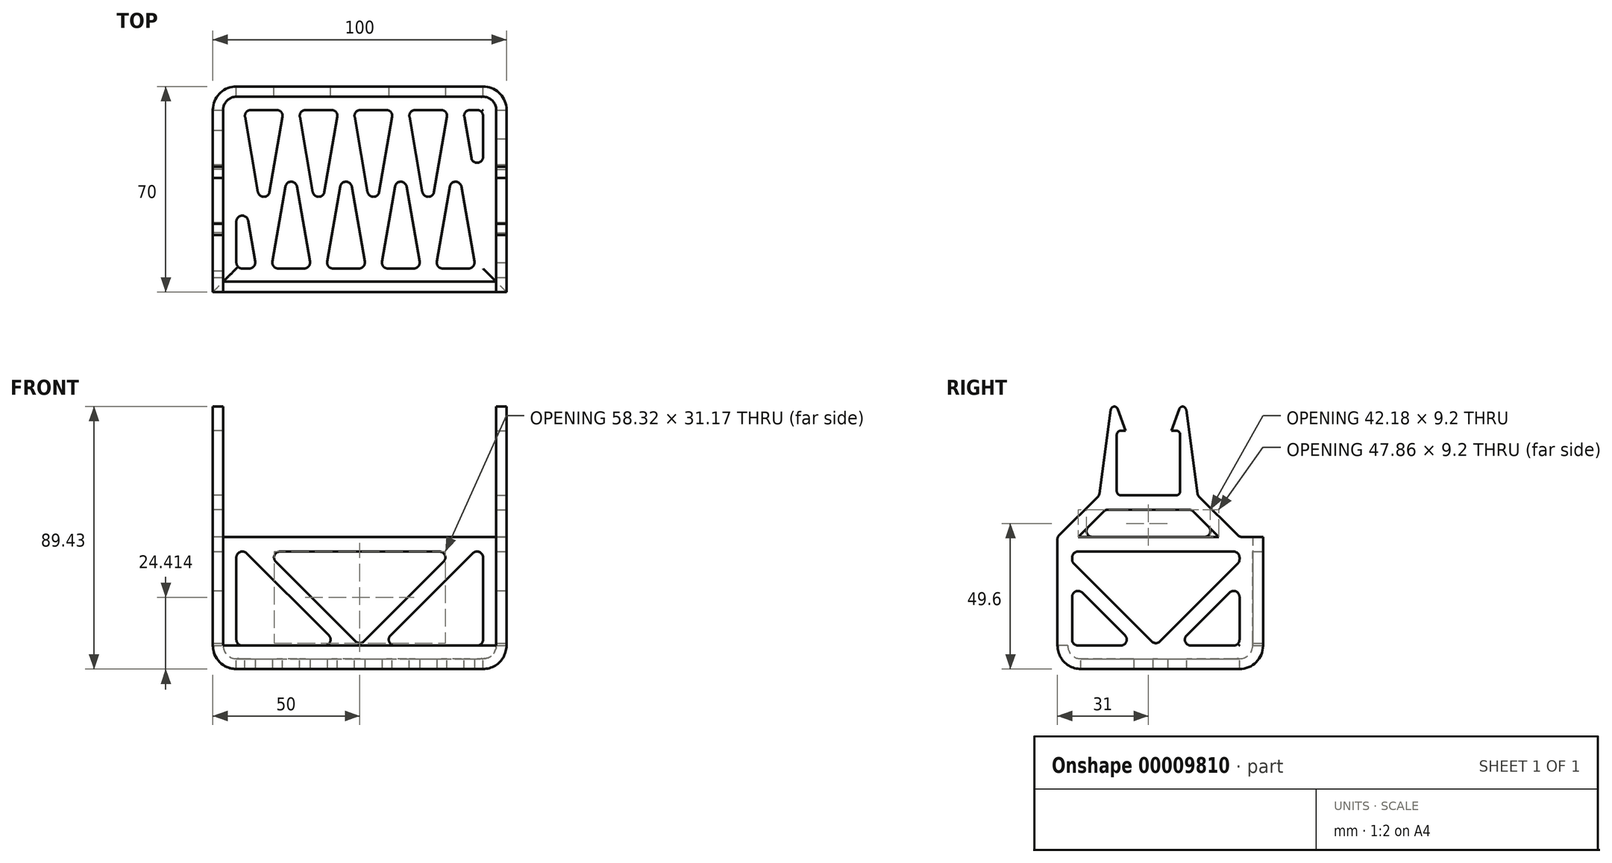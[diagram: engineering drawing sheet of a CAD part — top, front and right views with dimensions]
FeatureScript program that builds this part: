
annotation { "Feature Type Name" : "Feature", "Feature Type Description" : "" }
export const myFeature = defineFeature(function(context is Context, id is Id, definition is map)
    precondition{}
    {
        {
            var Q0;
            Q0=qCreatedBy(makeId("Top.planeOp"),FACE);
            var sketch = newSketch(context, id + "F0", { "sketchPlane" : qUnion([Q0])});
            skLineSegment(sketch, "E0.rect.bottom", {"start": v(50, 35) * mm, "end": v(-50, 35) * mm});
            skLineSegment(sketch, "E0.rect.top", {"start": v(50, -35) * mm, "end": v(-50, -35) * mm});
            skLineSegment(sketch, "E0.rect.left", {"start": v(50, 35) * mm, "end": v(50, -35) * mm});
            skLineSegment(sketch, "E0.rect.right", {"start": v(-50, 35) * mm, "end": v(-50, -35) * mm});
            skPoint(sketch, "E0.rect.middle", {"position": v(0, 0) * mm});
            skSolve(sketch);
        }
        {
            var Q0;
            Q0 = qSketchRegion(id + "F0", true);
            extrude(context, id + "F1", {"entities" : qUnion([Q0]), "depth" : 45 * mm});
        }
        {
            var Q0;
            Q0=makeQuery(id+"F1.opExtrude","CAP_FACE",FACE,{"disambiguationData":[OSD([sQuery(id+"F0.wireOp",EDGE,"E0.rect.bottom"),sQuery(id+"F0.wireOp",EDGE,"E0.rect.top"),sQuery(id+"F0.wireOp",EDGE,"E0.rect.left"),sQuery(id+"F0.wireOp",EDGE,"E0.rect.right")])],"isStart":true});
            var Q1;
            Q1=makeQuery(id+"F1.opExtrude","SWEPT_EDGE",EDGE,{"disambiguationData":[OSD([sQuery(id+"F0.wireOp",EDGE,"E0.rect.bottom"),sQuery(id+"F0.wireOp",EDGE,"E0.rect.left")])]});
            var Q2;
            Q2=makeQuery(id+"F1.opExtrude","SWEPT_EDGE",EDGE,{"disambiguationData":[OSD([sQuery(id+"F0.wireOp",EDGE,"E0.rect.bottom"),sQuery(id+"F0.wireOp",EDGE,"E0.rect.right")])]});
            fillet(context, id + "F2", {"entities" : qUnion([Q0, Q1, Q2]), "radius" : 8 * mm, "tangentPropagation" : true, "allowEdgeOverflow" : false});
        }
        {
            var Q0;
            Q0=makeQuery(id+"F1.opExtrude","CAP_FACE",FACE,{"disambiguationData":[OSD([sQuery(id+"F0.wireOp",EDGE,"E0.rect.bottom"),sQuery(id+"F0.wireOp",EDGE,"E0.rect.top"),sQuery(id+"F0.wireOp",EDGE,"E0.rect.left"),sQuery(id+"F0.wireOp",EDGE,"E0.rect.right")])],"isStart":false});
            shell(context, id + "F3", {"entities" : qUnion([Q0]), "thickness" : 3.5 * mm});
        }
        {
            var Q0;
            Q0=makeQuery(id+"F1.opExtrude","SWEPT_FACE",FACE,{"disambiguationData":[OSD([sQuery(id+"F0.wireOp",EDGE,"E0.rect.top")])]});
            var sketch = newSketch(context, id + "F4", { "sketchPlane" : qUnion([Q0])});
            skLineSegment(sketch, "E1.0", {"start": v(-46.5, 45) * mm, "end": v(-46.5, 8) * mm});
            skLineSegment(sketch, "E2.0", {"start": v(46.5, 8) * mm, "end": v(46.5, 45) * mm});
            skLineSegment(sketch, "E3", {"start": v(-46.5, 45) * mm, "end": v(46.5, 45) * mm});
            skLineSegment(sketch, "E4", {"start": v(46.5, 8) * mm, "end": v(-46.5, 8) * mm});
            skSolve(sketch);
        }
        {
            var Q0;
            {var subQ3=sQuery(id+"F4.wireOp",EDGE,"E1.0");Q0=makeQuery(id+"F4.imprint","IMPRINT",FACE,{"disambiguationData":[TD([[makeQuery(id+"F4.imprint","IMPRINT",EDGE,{"derivedFrom":subQ3}),1.0]])]});}
            var Q1;
            {var subQ0=sQuery(id+"F0.wireOp",EDGE,"E0.rect.top");var subQ1=makeQuery(id+"F1.opExtrude","SWEPT_FACE",FACE,{"disambiguationData":[OSD([subQ0])]});var subQ2=makeQuery(id+"F2.opFillet","BLEND_EDGE",EDGE,{"blendedFrom":[makeQuery(id+"F1.opExtrude","SWEPT_EDGE",EDGE,{"disambiguationData":[OSD([subQ0,sQuery(id+"F0.wireOp",EDGE,"E0.rect.left")])]}),subQ1],"blendedInto":[subQ1]});Q1=makeQuery(id+"F4.imprint","IMPRINT",FACE,{"disambiguationData":[TD([[makeQuery(id+"F4.imprint","IMPRINT",EDGE,{"derivedFrom":subQ2}),1.0]])]});}
            var Q2;
            {var subQ3=sQuery(id+"F4.wireOp",EDGE,"E2.0");Q2=makeQuery(id+"F4.imprint","IMPRINT",FACE,{"disambiguationData":[TD([[makeQuery(id+"F4.imprint","IMPRINT",EDGE,{"derivedFrom":subQ3}),1.0]])]});}
            extrude(context, id + "F5", {"entities" : qUnion([Q0, Q1, Q2]), "operationType" : NewBodyOperationType.REMOVE, "oppositeDirection" : true, "depth" : 25.4 * mm});
        }
        {
            var Q0;
            Q0=makeQuery(id+"F1.opExtrude","SWEPT_FACE",FACE,{"disambiguationData":[OSD([sQuery(id+"F0.wireOp",EDGE,"E0.rect.left")])]});
            var sketch = newSketch(context, id + "F6", { "sketchPlane" : qUnion([Q0])});
            skLineSegment(sketch, "E5", {"start": v(-30, 45) * mm, "end": v(-30, 8) * mm});
            skLineSegment(sketch, "E6", {"start": v(27, 45) * mm, "end": v(27, 8) * mm});
            skLineSegment(sketch, "E7", {"start": v(27, 8) * mm, "end": v(32, 8) * mm});
            skLineSegment(sketch, "E8", {"start": v(32, 8) * mm, "end": v(32, 45) * mm});
            skLineSegment(sketch, "E9", {"start": v(-35, 45) * mm, "end": v(-35, 8) * mm});
            skLineSegment(sketch, "E10", {"start": v(-35, 8) * mm, "end": v(-30, 8) * mm});
            skLineSegment(sketch, "E11", {"start": v(-30, 40) * mm, "end": v(27, 40) * mm});
            skLineSegment(sketch, "E12", {"start": v(27, 40) * mm, "end": v(27, 45) * mm});
            skLineSegment(sketch, "E13", {"start": v(-30, 8) * mm, "end": v(27, 8) * mm});
            skLineSegment(sketch, "E14", {"start": v(-1.5, 40) * mm, "end": v(-1.5, 8) * mm, "construction": true});
            skLineSegment(sketch, "E15", {"start": v(-1.5, 40) * mm, "end": v(-1.5, 45) * mm, "construction": true});
            skLineSegment(sketch, "E16", {"start": v(-1.5, 8) * mm, "end": v(-30, 36.5) * mm});
            skLineSegment(sketch, "E17", {"start": v(-8.57, 8) * mm, "end": v(-30, 29.43) * mm});
            skLineSegment(sketch, "E18", {"start": v(-15.75, 22.25) * mm, "end": v(-19.29, 18.71) * mm, "construction": true});
            skLineSegment(sketch, "E19", {"start": v(-1.5, 8) * mm, "end": v(27, 36.5) * mm});
            skLineSegment(sketch, "E20", {"start": v(5.57, 8) * mm, "end": v(27, 29.43) * mm});
            skLineSegment(sketch, "E21", {"start": v(12.75, 22.25) * mm, "end": v(16.29, 18.71) * mm, "construction": true});
            skSolve(sketch);
        }
        {
            var Q0;
            {var subQ0=sQuery(id+"F6.wireOp",EDGE,"E17");Q0=makeQuery(id+"F6.imprint","IMPRINT",FACE,{"disambiguationData":[TD([[makeQuery(id+"F6.imprint","IMPRINT",EDGE,{"derivedFrom":subQ0}),1.0]])]});}
            var Q1;
            {var subQ2=sQuery(id+"F6.wireOp",EDGE,"E11");Q1=makeQuery(id+"F6.imprint","IMPRINT",FACE,{"disambiguationData":[TD([[makeQuery(id+"F6.imprint","IMPRINT",EDGE,{"derivedFrom":subQ2}),-1.0]])]});}
            var Q2;
            {var subQ0=sQuery(id+"F6.wireOp",EDGE,"E20");Q2=makeQuery(id+"F6.imprint","IMPRINT",FACE,{"disambiguationData":[TD([[makeQuery(id+"F6.imprint","IMPRINT",EDGE,{"derivedFrom":subQ0}),-1.0]])]});}
            extrude(context, id + "F7", {"entities" : qUnion([Q0, Q1, Q2]), "operationType" : NewBodyOperationType.REMOVE, "endBound" : BoundingType.THROUGH_ALL, "oppositeDirection" : true, "depth" : 25.4 * mm});
        }
        {
            var Q0;
            Q0=makeQuery(id+"F1.opExtrude","SWEPT_FACE",FACE,{"disambiguationData":[OSD([sQuery(id+"F0.wireOp",EDGE,"E0.rect.bottom")])]});
            var sketch = newSketch(context, id + "F8", { "sketchPlane" : qUnion([Q0])});
            skLineSegment(sketch, "E22", {"start": v(-42, 45) * mm, "end": v(-42, 8) * mm});
            skLineSegment(sketch, "E23", {"start": v(-42, 8) * mm, "end": v(-47, 8) * mm});
            skLineSegment(sketch, "E24", {"start": v(-47, 8) * mm, "end": v(-47, 45) * mm});
            skLineSegment(sketch, "E25", {"start": v(-42, 45) * mm, "end": v(-42, 40) * mm});
            skLineSegment(sketch, "E26", {"start": v(-42, 40) * mm, "end": v(42, 40) * mm});
            skLineSegment(sketch, "E27", {"start": v(42, 40) * mm, "end": v(42, 45) * mm});
            skLineSegment(sketch, "E28", {"start": v(42, 45) * mm, "end": v(47, 45) * mm});
            skLineSegment(sketch, "E29", {"start": v(47, 45) * mm, "end": v(47, 8) * mm});
            skLineSegment(sketch, "E30", {"start": v(47, 8) * mm, "end": v(42, 8) * mm});
            skLineSegment(sketch, "E31", {"start": v(42, 8) * mm, "end": v(42, 40) * mm});
            skLineSegment(sketch, "E32", {"start": v(-42, 8) * mm, "end": v(42, 8) * mm});
            skLineSegment(sketch, "E33", {"start": v(-19.54, 20.46) * mm, "end": v(-16, 24) * mm, "construction": true});
            skLineSegment(sketch, "E34", {"start": v(16, 24) * mm, "end": v(19.54, 20.46) * mm, "construction": true});
            skLineSegment(sketch, "E35", {"start": v(0, 40) * mm, "end": v(0, 8) * mm, "construction": true});
            skLineSegment(sketch, "E36", {"start": v(0, 8) * mm, "end": v(-32, 40) * mm});
            skLineSegment(sketch, "E37", {"start": v(0, 8) * mm, "end": v(32, 40) * mm});
            skLineSegment(sketch, "E38", {"start": v(-7.07, 8) * mm, "end": v(-39.07, 40) * mm});
            skLineSegment(sketch, "E39", {"start": v(7.07, 8) * mm, "end": v(39.07, 40) * mm});
            skSolve(sketch);
        }
        {
            var Q0;
            {var subQ2=sQuery(id+"F8.wireOp",EDGE,"E22");Q0=makeQuery(id+"F8.imprint","IMPRINT",FACE,{"disambiguationData":[TD([[makeQuery(id+"F8.imprint","IMPRINT",EDGE,{"derivedFrom":subQ2}),1.0]])]});}
            var Q1;
            {var subQ1=sQuery(id+"F8.wireOp",EDGE,"E36");Q1=makeQuery(id+"F8.imprint","IMPRINT",FACE,{"disambiguationData":[TD([[makeQuery(id+"F8.imprint","IMPRINT",EDGE,{"derivedFrom":subQ1}),-1.0]])]});}
            var Q2;
            {var subQ2=sQuery(id+"F8.wireOp",EDGE,"E31");Q2=makeQuery(id+"F8.imprint","IMPRINT",FACE,{"disambiguationData":[TD([[makeQuery(id+"F8.imprint","IMPRINT",EDGE,{"derivedFrom":subQ2}),1.0]])]});}
            extrude(context, id + "F9", {"entities" : qUnion([Q0, Q1, Q2]), "operationType" : NewBodyOperationType.REMOVE, "endBound" : BoundingType.THROUGH_ALL, "oppositeDirection" : true, "depth" : 25 * mm});
        }
        {
            var Q0;
            Q0=makeQuery(id+"F3.opShell","OFFSET_FACE",FACE,{"disambiguationData":[OSD([sQuery(id+"F0.wireOp",EDGE,"E0.rect.bottom"),sQuery(id+"F0.wireOp",EDGE,"E0.rect.top"),sQuery(id+"F0.wireOp",EDGE,"E0.rect.left"),sQuery(id+"F0.wireOp",EDGE,"E0.rect.right")])]});
            var sketch = newSketch(context, id + "F10", { "sketchPlane" : qUnion([Q0])});
            skLineSegment(sketch, "E40.left", {"start": v(-42, -27) * mm, "end": v(-42, 27) * mm});
            skLineSegment(sketch, "E40.right", {"start": v(42, -27) * mm, "end": v(42, 27) * mm});
            skLineSegment(sketch, "E41", {"start": v(-42, 27) * mm, "end": v(-32.67, -27) * mm, "construction": true});
            skLineSegment(sketch, "E42", {"start": v(-32.67, -27) * mm, "end": v(-23.33, 27) * mm, "construction": true});
            skLineSegment(sketch, "E43", {"start": v(-23.33, 27) * mm, "end": v(-14, -27) * mm, "construction": true});
            skLineSegment(sketch, "E44", {"start": v(-14, -27) * mm, "end": v(-4.67, 27) * mm, "construction": true});
            skLineSegment(sketch, "E45", {"start": v(-4.67, 27) * mm, "end": v(4.67, -27) * mm, "construction": true});
            skLineSegment(sketch, "E46", {"start": v(4.67, -27) * mm, "end": v(14, 27) * mm, "construction": true});
            skLineSegment(sketch, "E47", {"start": v(14, 27) * mm, "end": v(23.33, -27) * mm, "construction": true});
            skLineSegment(sketch, "E48.0", {"start": v(14, 12.32) * mm, "end": v(20.8, -27) * mm});
            skLineSegment(sketch, "E48.1", {"start": v(7.2, -27) * mm, "end": v(14, 12.32) * mm});
            skLineSegment(sketch, "E48.2", {"start": v(-4.67, 12.32) * mm, "end": v(2.13, -27) * mm});
            skLineSegment(sketch, "E48.3", {"start": v(-11.46, -27) * mm, "end": v(-4.67, 12.32) * mm});
            skLineSegment(sketch, "E48.4", {"start": v(-23.33, 12.32) * mm, "end": v(-16.54, -27) * mm});
            skLineSegment(sketch, "E48.5", {"start": v(-30.13, -27) * mm, "end": v(-23.33, 12.32) * mm});
            skLineSegment(sketch, "E48.6", {"start": v(-42, 12.32) * mm, "end": v(-35.2, -27) * mm});
            skLineSegment(sketch, "E49.0", {"start": v(16.54, 27) * mm, "end": v(23.33, -12.32) * mm});
            skLineSegment(sketch, "E49.1", {"start": v(4.67, -12.32) * mm, "end": v(11.46, 27) * mm});
            skLineSegment(sketch, "E49.2", {"start": v(-2.13, 27) * mm, "end": v(4.67, -12.32) * mm});
            skLineSegment(sketch, "E49.3", {"start": v(-14, -12.32) * mm, "end": v(-7.2, 27) * mm});
            skLineSegment(sketch, "E49.4", {"start": v(-20.8, 27) * mm, "end": v(-14, -12.32) * mm});
            skLineSegment(sketch, "E49.5", {"start": v(-32.67, -12.32) * mm, "end": v(-25.87, 27) * mm});
            skLineSegment(sketch, "E49.6", {"start": v(-39.46, 27) * mm, "end": v(-32.67, -12.32) * mm});
            skLineSegment(sketch, "E50", {"start": v(-32.67, -12.32) * mm, "end": v(-32.67, 27) * mm, "construction": true});
            skLineSegment(sketch, "E51", {"start": v(-23.33, 12.32) * mm, "end": v(-23.33, -27) * mm, "construction": true});
            skLineSegment(sketch, "E52", {"start": v(-14, -12.32) * mm, "end": v(-14, 27) * mm, "construction": true});
            skLineSegment(sketch, "E53", {"start": v(-4.67, 12.32) * mm, "end": v(-4.67, -27) * mm, "construction": true});
            skLineSegment(sketch, "E54", {"start": v(4.67, -12.32) * mm, "end": v(4.67, 27) * mm, "construction": true});
            skLineSegment(sketch, "E55", {"start": v(14, 12.32) * mm, "end": v(14, -27) * mm, "construction": true});
            skLineSegment(sketch, "E56", {"start": v(23.33, -27) * mm, "end": v(32.67, 27) * mm, "construction": true});
            skLineSegment(sketch, "E57", {"start": v(32.67, 27) * mm, "end": v(42, -27) * mm, "construction": true});
            skLineSegment(sketch, "E58.0", {"start": v(32.67, 12.32) * mm, "end": v(39.46, -27) * mm});
            skLineSegment(sketch, "E58.1", {"start": v(25.87, -27) * mm, "end": v(32.67, 12.32) * mm});
            skLineSegment(sketch, "E59", {"start": v(23.33, -12.32) * mm, "end": v(30.13, 27) * mm});
            skLineSegment(sketch, "E60", {"start": v(35.2, 27) * mm, "end": v(42, -12.32) * mm});
            skSolve(sketch);
        }
        {
            var Q0;
            {var subQ6=sQuery(id+"F10.wireOp",EDGE,"E49.5");Q0=makeQuery(id+"F10.imprint","IMPRINT",FACE,{"disambiguationData":[TD([[makeQuery(id+"F10.imprint","IMPRINT",EDGE,{"derivedFrom":subQ6}),1.0]])]});}
            var Q1;
            {var subQ0=sQuery(id+"F10.wireOp",EDGE,"E48.6");Q1=makeQuery(id+"F10.imprint","IMPRINT",FACE,{"disambiguationData":[TD([[makeQuery(id+"F10.imprint","IMPRINT",EDGE,{"derivedFrom":subQ0}),-1.0]])]});}
            var Q2;
            {var subQ6=sQuery(id+"F10.wireOp",EDGE,"E48.4");Q2=makeQuery(id+"F10.imprint","IMPRINT",FACE,{"disambiguationData":[TD([[makeQuery(id+"F10.imprint","IMPRINT",EDGE,{"derivedFrom":subQ6}),-1.0]])]});}
            var Q3;
            {var subQ6=sQuery(id+"F10.wireOp",EDGE,"E49.3");Q3=makeQuery(id+"F10.imprint","IMPRINT",FACE,{"disambiguationData":[TD([[makeQuery(id+"F10.imprint","IMPRINT",EDGE,{"derivedFrom":subQ6}),1.0]])]});}
            var Q4;
            {var subQ6=sQuery(id+"F10.wireOp",EDGE,"E48.2");Q4=makeQuery(id+"F10.imprint","IMPRINT",FACE,{"disambiguationData":[TD([[makeQuery(id+"F10.imprint","IMPRINT",EDGE,{"derivedFrom":subQ6}),-1.0]])]});}
            var Q5;
            {var subQ6=sQuery(id+"F10.wireOp",EDGE,"E49.1");Q5=makeQuery(id+"F10.imprint","IMPRINT",FACE,{"disambiguationData":[TD([[makeQuery(id+"F10.imprint","IMPRINT",EDGE,{"derivedFrom":subQ6}),1.0]])]});}
            var Q6;
            {var subQ6=sQuery(id+"F10.wireOp",EDGE,"E48.0");Q6=makeQuery(id+"F10.imprint","IMPRINT",FACE,{"disambiguationData":[TD([[makeQuery(id+"F10.imprint","IMPRINT",EDGE,{"derivedFrom":subQ6}),-1.0]])]});}
            var Q7;
            {var subQ6=sQuery(id+"F10.wireOp",EDGE,"E49.0");Q7=makeQuery(id+"F10.imprint","IMPRINT",FACE,{"disambiguationData":[TD([[makeQuery(id+"F10.imprint","IMPRINT",EDGE,{"derivedFrom":subQ6}),1.0]])]});}
            var Q8;
            {var subQ6=sQuery(id+"F10.wireOp",EDGE,"E58.0");Q8=makeQuery(id+"F10.imprint","IMPRINT",FACE,{"disambiguationData":[TD([[makeQuery(id+"F10.imprint","IMPRINT",EDGE,{"derivedFrom":subQ6}),-1.0]])]});}
            var Q9;
            {var subQ5=sQuery(id+"F10.wireOp",EDGE,"E60");Q9=makeQuery(id+"F10.imprint","IMPRINT",FACE,{"disambiguationData":[TD([[makeQuery(id+"F10.imprint","IMPRINT",EDGE,{"derivedFrom":subQ5}),1.0]])]});}
            extrude(context, id + "F11", {"entities" : qUnion([Q0, Q1, Q2, Q3, Q4, Q5, Q6, Q7, Q8, Q9]), "operationType" : NewBodyOperationType.REMOVE, "endBound" : BoundingType.THROUGH_ALL, "oppositeDirection" : true, "depth" : 25 * mm});
        }
        {
            var Q0;
            Q0=makeQuery(id+"FnaAj31UVdTN3sp_1.opFillet","SPLIT",FACE,{"disambiguationData":[OD(12.0)],"derivedFrom":makeQuery(id+"F1.opExtrude","SWEPT_FACE",FACE,{"disambiguationData":[OSD([sQuery(id+"F0.wireOp",EDGE,"E0.rect.right")])]})});
            var sketch = newSketch(context, id + "F12", { "sketchPlane" : qUnion([Q0])});
            skLineSegment(sketch, "E61", {"start": v(-27, 45) * mm, "end": v(35, 45) * mm});
            skLineSegment(sketch, "E62", {"start": v(35, 45) * mm, "end": v(20.8, 59.2) * mm});
            skLineSegment(sketch, "E63", {"start": v(-12.8, 59.2) * mm, "end": v(-27, 45) * mm});
            skLineSegment(sketch, "E64", {"start": v(-19.93, 45) * mm, "end": v(-10.73, 54.2) * mm});
            skLineSegment(sketch, "E65", {"start": v(-10.73, 54.2) * mm, "end": v(18.73, 54.2) * mm});
            skLineSegment(sketch, "E66", {"start": v(18.73, 54.2) * mm, "end": v(27.93, 45) * mm});
            skLineSegment(sketch, "E67", {"start": v(4, 59.2) * mm, "end": v(4, 54.2) * mm, "construction": true});
            skLineSegment(sketch, "E68", {"start": v(-19.9, 52.1) * mm, "end": v(-16.36, 48.56) * mm, "construction": true});
            skLineSegment(sketch, "E69", {"start": v(27.9, 52.1) * mm, "end": v(24.36, 48.56) * mm, "construction": true});
            skLineSegment(sketch, "E70", {"start": v(-12.8, 59.2) * mm, "end": v(-8.68, 89.44) * mm});
            skLineSegment(sketch, "E71", {"start": v(20.8, 59.2) * mm, "end": v(16.68, 89.44) * mm});
            skLineSegment(sketch, "E72", {"start": v(-6.8, 59.2) * mm, "end": v(-6.8, 89.44) * mm});
            skLineSegment(sketch, "E73", {"start": v(14.8, 59.2) * mm, "end": v(14.8, 89.44) * mm});
            skLineSegment(sketch, "E74", {"start": v(-8.68, 89.44) * mm, "end": v(-6.8, 89.44) * mm});
            skLineSegment(sketch, "E75", {"start": v(14.8, 89.44) * mm, "end": v(16.68, 89.44) * mm});
            skLineSegment(sketch, "E76", {"start": v(-3.8, 81.2) * mm, "end": v(-6.8, 81.2) * mm});
            skLineSegment(sketch, "E77", {"start": v(11.8, 81.2) * mm, "end": v(14.8, 81.2) * mm});
            skLineSegment(sketch, "E78", {"start": v(-12.8, 59.2) * mm, "end": v(-6.8, 59.2) * mm});
            skLineSegment(sketch, "E79", {"start": v(-6.8, 59.2) * mm, "end": v(14.8, 59.2) * mm});
            skLineSegment(sketch, "E80", {"start": v(14.8, 59.2) * mm, "end": v(20.8, 59.2) * mm});
            skLineSegment(sketch, "E81", {"start": v(-6.8, 89.44) * mm, "end": v(-3.8, 81.2) * mm});
            skLineSegment(sketch, "E82", {"start": v(11.8, 81.2) * mm, "end": v(14.8, 89.44) * mm});
            skLineSegment(sketch, "E83", {"start": v(-6.8, 81.2) * mm, "end": v(-9.8, 81.2) * mm, "construction": true});
            skSolve(sketch);
        }
        {
            var Q0;
            {var subQ6=sQuery(id+"F12.wireOp",EDGE,"E62");Q0=makeQuery(id+"F12.imprint","IMPRINT",FACE,{"disambiguationData":[TD([[makeQuery(id+"F12.imprint","IMPRINT",EDGE,{"derivedFrom":subQ6}),1.0]])]});}
            var Q1;
            {var subQ5=sQuery(id+"F12.wireOp",EDGE,"E71");Q1=makeQuery(id+"F12.imprint","IMPRINT",FACE,{"disambiguationData":[TD([[makeQuery(id+"F12.imprint","IMPRINT",EDGE,{"derivedFrom":subQ5}),1.0]])]});}
            var Q2;
            {var subQ5=sQuery(id+"F12.wireOp",EDGE,"E70");Q2=makeQuery(id+"F12.imprint","IMPRINT",FACE,{"disambiguationData":[TD([[makeQuery(id+"F12.imprint","IMPRINT",EDGE,{"derivedFrom":subQ5}),-1.0]])]});}
            var Q3;
            {var subQ1=sQuery(id+"F12.wireOp",EDGE,"22c29fa1-6a54-4cfb-86ce-f89d12a1b06d");Q3=makeQuery(id+"F12.imprint","IMPRINT",FACE,{"disambiguationData":[TD([[makeQuery(id+"F12.imprint","IMPRINT",EDGE,{"derivedFrom":subQ1}),1.0]])]});}
            var Q4;
            {var subQ1=sQuery(id+"F12.wireOp",EDGE,"e746244f-2f82-4b7e-aadf-d7acfe26c637");Q4=makeQuery(id+"F12.imprint","IMPRINT",FACE,{"disambiguationData":[TD([[makeQuery(id+"F12.imprint","IMPRINT",EDGE,{"derivedFrom":subQ1}),-1.0]])]});}
            var Q5;
            {var subQ1=sQuery(id+"F12.wireOp",EDGE,"E76");Q5=makeQuery(id+"F12.imprint","IMPRINT",FACE,{"disambiguationData":[TD([[makeQuery(id+"F12.imprint","IMPRINT",EDGE,{"derivedFrom":subQ1}),-1.0]])]});}
            var Q6;
            {var subQ1=sQuery(id+"F12.wireOp",EDGE,"E77");Q6=makeQuery(id+"F12.imprint","IMPRINT",FACE,{"disambiguationData":[TD([[makeQuery(id+"F12.imprint","IMPRINT",EDGE,{"derivedFrom":subQ1}),1.0]])]});}
            var Q7;
            {var subQ0=sQuery(id+"F0.wireOp",EDGE,"E0.rect.right");Q7=makeQuery(id+"FnaAj31UVdTN3sp_1.opFillet","SPLIT",FACE,{"disambiguationData":[OD(14.0)],"derivedFrom":makeQuery(id+"F5.boolean.opBoolean","MERGE",FACE,{"derivedFrom":[makeQuery(id+"F3.opShell","OFFSET_FACE",FACE,{"disambiguationData":[OSD([subQ0]),TDD([makeQuery(id+"F1.opExtrude","SWEPT_FACE",FACE,{"disambiguationData":[OSD([subQ0])]})])]}),makeQuery(id+"F5.opExtrude","SWEPT_FACE",FACE,{"disambiguationData":[OSD([sQuery(id+"F4.wireOp",EDGE,"E1.0")])]})]})});}
            extrude(context, id + "F13", {"entities" : qUnion([Q0, Q1, Q2, Q3, Q4, Q5, Q6]), "endBound" : BoundingType.UP_TO_SURFACE, "oppositeDirection" : true, "endBoundEntityFace" : qUnion([Q7]), "depth" : 25 * mm});
        }
        {
            var Q0;
            Q0=makeQuery(id+"F13.opExtrude","SWEPT_EDGE",EDGE,{"disambiguationData":[OSD([sQuery(id+"F12.wireOp",EDGE,"E72"),sQuery(id+"F12.wireOp",EDGE,"E76")])]});
            var Q1;
            Q1=makeQuery(id+"F13.opExtrude","SWEPT_EDGE",EDGE,{"disambiguationData":[OSD([sQuery(id+"F12.wireOp",EDGE,"E73"),sQuery(id+"F12.wireOp",EDGE,"E77")])]});
            var Q2;
            Q2=makeQuery(id+"F13.opExtrude","SWEPT_EDGE",EDGE,{"disambiguationData":[OSD([sQuery(id+"F12.wireOp",EDGE,"E73"),sQuery(id+"F12.wireOp",EDGE,"E77")])]});
            var Q3;
            Q3=makeQuery(id+"F13.opExtrude","SWEPT_EDGE",EDGE,{"disambiguationData":[OSD([sQuery(id+"F12.wireOp",EDGE,"E72"),sQuery(id+"F12.wireOp",EDGE,"E76")])]});
            var Q4;
            Q4=makeQuery(id+"F13.opExtrude","SWEPT_EDGE",EDGE,{"disambiguationData":[OSD([sQuery(id+"F12.wireOp",EDGE,"E72"),sQuery(id+"F12.wireOp",EDGE,"E76")])]});
            var Q5;
            Q5=makeQuery(id+"F13.opExtrude","SWEPT_EDGE",EDGE,{"disambiguationData":[OSD([sQuery(id+"F12.wireOp",EDGE,"E73"),sQuery(id+"F12.wireOp",EDGE,"E77")])]});
            var Q6;
            Q6=makeQuery(id+"F13.opExtrude","SWEPT_EDGE",EDGE,{"disambiguationData":[OSD([sQuery(id+"F12.wireOp",EDGE,"E70"),sQuery(id+"F12.wireOp",EDGE,"E74")])]});
            var Q7;
            Q7=makeQuery(id+"F13.opExtrude","SWEPT_EDGE",EDGE,{"disambiguationData":[OSD([sQuery(id+"F12.wireOp",EDGE,"E71"),sQuery(id+"F12.wireOp",EDGE,"E75")])]});
            var Q8;
            Q8=makeQuery(id+"F13.opExtrude","SWEPT_EDGE",EDGE,{"disambiguationData":[OSD([sQuery(id+"F12.wireOp",EDGE,"E62"),sQuery(id+"F12.wireOp",EDGE,"E71"),sQuery(id+"F12.wireOp",EDGE,"E80")])]});
            var Q9;
            Q9=makeQuery(id+"F13.opExtrude","SWEPT_EDGE",EDGE,{"disambiguationData":[OSD([sQuery(id+"F12.wireOp",EDGE,"E63"),sQuery(id+"F12.wireOp",EDGE,"E70"),sQuery(id+"F12.wireOp",EDGE,"E78")])]});
            var Q10;
            Q10=makeQuery(id+"F13.opExtrude","SWEPT_EDGE",EDGE,{"disambiguationData":[OSD([sQuery(id+"F12.wireOp",EDGE,"E64"),sQuery(id+"F12.wireOp",EDGE,"E65")])]});
            var Q11;
            Q11=makeQuery(id+"F13.opExtrude","SWEPT_EDGE",EDGE,{"disambiguationData":[OSD([sQuery(id+"F12.wireOp",EDGE,"E65"),sQuery(id+"F12.wireOp",EDGE,"E66")])]});
            var Q12;
            Q12=makeQuery(id+"F13.opExtrude","SWEPT_EDGE",EDGE,{"disambiguationData":[OSD([sQuery(id+"F12.wireOp",EDGE,"E72"),sQuery(id+"F12.wireOp",EDGE,"E74"),sQuery(id+"F12.wireOp",EDGE,"E81")])]});
            var Q13;
            Q13=makeQuery(id+"F13.opExtrude","SWEPT_EDGE",EDGE,{"disambiguationData":[OSD([sQuery(id+"F12.wireOp",EDGE,"E73"),sQuery(id+"F12.wireOp",EDGE,"E75"),sQuery(id+"F12.wireOp",EDGE,"E82")])]});
            var Q14;
            Q14=makeQuery(id+"F13.opExtrude","SWEPT_EDGE",EDGE,{"disambiguationData":[OSD([sQuery(id+"F12.wireOp",EDGE,"E73"),sQuery(id+"F12.wireOp",EDGE,"E79"),sQuery(id+"F12.wireOp",EDGE,"E80")])]});
            var Q15;
            Q15=makeQuery(id+"F13.opExtrude","SWEPT_EDGE",EDGE,{"disambiguationData":[OSD([sQuery(id+"F12.wireOp",EDGE,"E72"),sQuery(id+"F12.wireOp",EDGE,"E78"),sQuery(id+"F12.wireOp",EDGE,"E79")])]});
            fillet(context, id + "F14", {"entities" : qUnion([Q0, Q1, Q2, Q3, Q4, Q5, Q6, Q7, Q8, Q9, Q10, Q11, Q12, Q13, Q14, Q15]), "radius" : 1.4 * mm, "tangentPropagation" : true, "allowEdgeOverflow" : false});
        }
        {
            var Q0;
            Q0=makeQuery(id+"F13.opExtrude","SWEPT_BODY",BODY,{"disambiguationData":[OSD([sQuery(id+"F12.wireOp",EDGE,"E61"),sQuery(id+"F12.wireOp",EDGE,"E62"),sQuery(id+"F12.wireOp",EDGE,"f61140bf-b283-4cfe-8c45-a947c4cfa1a1"),sQuery(id+"F12.wireOp",EDGE,"E63"),sQuery(id+"F12.wireOp",EDGE,"E64"),sQuery(id+"F12.wireOp",EDGE,"E65"),sQuery(id+"F12.wireOp",EDGE,"E66"),sQuery(id+"F12.wireOp",EDGE,"E70"),sQuery(id+"F12.wireOp",EDGE,"E71"),sQuery(id+"F12.wireOp",EDGE,"E72"),sQuery(id+"F12.wireOp",EDGE,"E73"),sQuery(id+"F12.wireOp",EDGE,"E74"),sQuery(id+"F12.wireOp",EDGE,"E75"),sQuery(id+"F12.wireOp",EDGE,"e746244f-2f82-4b7e-aadf-d7acfe26c637"),sQuery(id+"F12.wireOp",EDGE,"2c4e8129-7896-41df-a1a4-87bb63dce362"),sQuery(id+"F12.wireOp",EDGE,"E76"),sQuery(id+"F12.wireOp",EDGE,"22c29fa1-6a54-4cfb-86ce-f89d12a1b06d"),sQuery(id+"F12.wireOp",EDGE,"f6f2a737-0b99-49e8-832f-f3440352c085"),sQuery(id+"F12.wireOp",EDGE,"E77")])]});
            var Q1;
            Q1=qCreatedBy(makeId("Right.planeOp"),FACE);
            mirror(context, id + "F15", {"operationType" : NewBodyOperationType.ADD, "entities" : qUnion([Q0]), "mirrorPlane" : qUnion([Q1])});
        }
        {
            var Q0;
            Q0=makeQuery(id+"F13.opExtrude","SWEPT_EDGE",EDGE,{"disambiguationData":[OSD([sQuery(id+"F0.wireOp",EDGE,"E0.rect.top"),sQuery(id+"F0.wireOp",EDGE,"E0.rect.right"),sQuery(id+"F12.wireOp",EDGE,"E61"),sQuery(id+"F12.wireOp",EDGE,"E62")])]});
            var Q1;
            Q1=makeQuery(id+"F13.opExtrude","SWEPT_EDGE",EDGE,{"disambiguationData":[OSD([sQuery(id+"F12.wireOp",EDGE,"E61"),sQuery(id+"F12.wireOp",EDGE,"E66")])]});
            var Q2;
            Q2=makeQuery(id+"F13.opExtrude","SWEPT_EDGE",EDGE,{"disambiguationData":[OSD([sQuery(id+"F12.wireOp",EDGE,"E61"),sQuery(id+"F12.wireOp",EDGE,"E64")])]});
            var Q3;
            Q3=makeQuery(id+"F13.opExtrude","SWEPT_EDGE",EDGE,{"disambiguationData":[OSD([sQuery(id+"F0.wireOp",EDGE,"E0.rect.bottom"),sQuery(id+"F0.wireOp",EDGE,"E0.rect.right"),sQuery(id+"F12.wireOp",EDGE,"E61"),sQuery(id+"F12.wireOp",EDGE,"E63")])]});
            var Q4;
            Q4=makeQuery(id+"F15.opPattern","COPY",EDGE,{"derivedFrom":makeQuery(id+"F13.opExtrude","SWEPT_EDGE",EDGE,{"disambiguationData":[OSD([sQuery(id+"F12.wireOp",EDGE,"E61"),sQuery(id+"F12.wireOp",EDGE,"E64")])]}),"instanceName":"1"});
            var Q5;
            Q5=makeQuery(id+"F15.opPattern","COPY",EDGE,{"derivedFrom":makeQuery(id+"F13.opExtrude","SWEPT_EDGE",EDGE,{"disambiguationData":[OSD([sQuery(id+"F0.wireOp",EDGE,"E0.rect.top"),sQuery(id+"F0.wireOp",EDGE,"E0.rect.right"),sQuery(id+"F12.wireOp",EDGE,"E61"),sQuery(id+"F12.wireOp",EDGE,"E62")])]}),"instanceName":"1"});
            var Q6;
            Q6=makeQuery(id+"F15.opPattern","COPY",EDGE,{"derivedFrom":makeQuery(id+"F13.opExtrude","SWEPT_EDGE",EDGE,{"disambiguationData":[OSD([sQuery(id+"F12.wireOp",EDGE,"E61"),sQuery(id+"F12.wireOp",EDGE,"E66")])]}),"instanceName":"1"});
            var Q7;
            Q7=makeQuery(id+"F15.opPattern","COPY",EDGE,{"derivedFrom":makeQuery(id+"F13.opExtrude","SWEPT_EDGE",EDGE,{"disambiguationData":[OSD([sQuery(id+"F0.wireOp",EDGE,"E0.rect.bottom"),sQuery(id+"F0.wireOp",EDGE,"E0.rect.right"),sQuery(id+"F12.wireOp",EDGE,"E61"),sQuery(id+"F12.wireOp",EDGE,"E63")])]}),"instanceName":"1"});
            fillet(context, id + "F16", {"entities" : qUnion([Q0, Q1, Q2, Q3, Q4, Q5, Q6, Q7]), "radius" : 2 * mm, "tangentPropagation" : true, "allowEdgeOverflow" : false});
        }
        {
            var Q0;
            Q0=makeQuery(id+"F9.boolean.opBoolean","COPY",EDGE,{"derivedFrom":makeQuery(id+"F9.opExtrude","SWEPT_EDGE",EDGE,{"disambiguationData":[OSD([sQuery(id+"F8.wireOp",EDGE,"E32"),sQuery(id+"F8.wireOp",EDGE,"21a8909e-d1f1-48ab-95bf-b171e8dcea50")])]})});
            var Q1;
            Q1=makeQuery(id+"F9.boolean.opBoolean","COPY",EDGE,{"derivedFrom":makeQuery(id+"F9.opExtrude","SWEPT_EDGE",EDGE,{"disambiguationData":[OSD([sQuery(id+"F8.wireOp",EDGE,"E32"),sQuery(id+"F8.wireOp",EDGE,"1ba8cede-bd71-4284-a01c-5ff4ff7b9d74")])]})});
            var Q2;
            Q2=makeQuery(id+"F9.boolean.opBoolean","COPY",EDGE,{"derivedFrom":makeQuery(id+"F9.opExtrude","SWEPT_EDGE",EDGE,{"disambiguationData":[OSD([sQuery(id+"F8.wireOp",EDGE,"E26"),sQuery(id+"F8.wireOp",EDGE,"ea21bc87-49c2-4c7b-8e74-a24736ba1dfa")])]})});
            var Q3;
            Q3=makeQuery(id+"F9.boolean.opBoolean","COPY",EDGE,{"derivedFrom":makeQuery(id+"F9.opExtrude","SWEPT_EDGE",EDGE,{"disambiguationData":[OSD([sQuery(id+"F8.wireOp",EDGE,"E26"),sQuery(id+"F8.wireOp",EDGE,"169d5384-7eed-4124-bf46-ad3f299ae7b2")])]})});
            var Q4;
            Q4=makeQuery(id+"F11.boolean.opBoolean","COPY",EDGE,{"derivedFrom":makeQuery(id+"F11.opExtrude","SWEPT_EDGE",EDGE,{"disambiguationData":[OSD([sQuery(id+"F10.wireOp",EDGE,"E49.5"),sQuery(id+"F10.wireOp",EDGE,"E49.6")])]})});
            var Q5;
            Q5=makeQuery(id+"F11.boolean.opBoolean","COPY",EDGE,{"derivedFrom":makeQuery(id+"F11.opExtrude","SWEPT_EDGE",EDGE,{"disambiguationData":[OSD([sQuery(id+"F0.wireOp",EDGE,"E0.rect.bottom"),sQuery(id+"F0.wireOp",EDGE,"E0.rect.top"),sQuery(id+"F0.wireOp",EDGE,"E0.rect.left"),sQuery(id+"F0.wireOp",EDGE,"E0.rect.right"),sQuery(id+"F10.wireOp",EDGE,"E40.left")])]})});
            var Q6;
            Q6=makeQuery(id+"F11.boolean.opBoolean","COPY",EDGE,{"derivedFrom":makeQuery(id+"F11.opExtrude","SWEPT_EDGE",EDGE,{"disambiguationData":[OSD([sQuery(id+"F0.wireOp",EDGE,"E0.rect.bottom"),sQuery(id+"F0.wireOp",EDGE,"E0.rect.top"),sQuery(id+"F0.wireOp",EDGE,"E0.rect.left"),sQuery(id+"F0.wireOp",EDGE,"E0.rect.right"),sQuery(id+"F10.wireOp",EDGE,"E48.6")])]})});
            var Q7;
            Q7=makeQuery(id+"F11.boolean.opBoolean","COPY",EDGE,{"derivedFrom":makeQuery(id+"F11.opExtrude","SWEPT_EDGE",EDGE,{"disambiguationData":[OSD([sQuery(id+"F0.wireOp",EDGE,"E0.rect.bottom"),sQuery(id+"F0.wireOp",EDGE,"E0.rect.top"),sQuery(id+"F0.wireOp",EDGE,"E0.rect.left"),sQuery(id+"F0.wireOp",EDGE,"E0.rect.right"),sQuery(id+"F10.wireOp",EDGE,"E48.5")])]})});
            var Q8;
            Q8=makeQuery(id+"F11.boolean.opBoolean","COPY",EDGE,{"derivedFrom":makeQuery(id+"F11.opExtrude","SWEPT_EDGE",EDGE,{"disambiguationData":[OSD([sQuery(id+"F0.wireOp",EDGE,"E0.rect.bottom"),sQuery(id+"F0.wireOp",EDGE,"E0.rect.top"),sQuery(id+"F0.wireOp",EDGE,"E0.rect.left"),sQuery(id+"F0.wireOp",EDGE,"E0.rect.right"),sQuery(id+"F10.wireOp",EDGE,"E48.3")])]})});
            var Q9;
            Q9=makeQuery(id+"F11.boolean.opBoolean","COPY",EDGE,{"derivedFrom":makeQuery(id+"F11.opExtrude","SWEPT_EDGE",EDGE,{"disambiguationData":[OSD([sQuery(id+"F0.wireOp",EDGE,"E0.rect.bottom"),sQuery(id+"F0.wireOp",EDGE,"E0.rect.top"),sQuery(id+"F0.wireOp",EDGE,"E0.rect.left"),sQuery(id+"F0.wireOp",EDGE,"E0.rect.right"),sQuery(id+"F10.wireOp",EDGE,"E48.1")])]})});
            var Q10;
            Q10=makeQuery(id+"F11.boolean.opBoolean","COPY",EDGE,{"derivedFrom":makeQuery(id+"F11.opExtrude","SWEPT_EDGE",EDGE,{"disambiguationData":[OSD([sQuery(id+"F0.wireOp",EDGE,"E0.rect.bottom"),sQuery(id+"F0.wireOp",EDGE,"E0.rect.top"),sQuery(id+"F0.wireOp",EDGE,"E0.rect.left"),sQuery(id+"F0.wireOp",EDGE,"E0.rect.right"),sQuery(id+"F10.wireOp",EDGE,"E58.1")])]})});
            var Q11;
            Q11=makeQuery(id+"F11.boolean.opBoolean","COPY",EDGE,{"derivedFrom":makeQuery(id+"F11.opExtrude","SWEPT_EDGE",EDGE,{"disambiguationData":[OSD([sQuery(id+"F10.wireOp",EDGE,"E49.3"),sQuery(id+"F10.wireOp",EDGE,"E49.4")])]})});
            var Q12;
            Q12=makeQuery(id+"F11.boolean.opBoolean","COPY",EDGE,{"derivedFrom":makeQuery(id+"F11.opExtrude","SWEPT_EDGE",EDGE,{"disambiguationData":[OSD([sQuery(id+"F10.wireOp",EDGE,"E49.1"),sQuery(id+"F10.wireOp",EDGE,"E49.2")])]})});
            var Q13;
            Q13=makeQuery(id+"F11.boolean.opBoolean","COPY",EDGE,{"derivedFrom":makeQuery(id+"F11.opExtrude","SWEPT_EDGE",EDGE,{"disambiguationData":[OSD([sQuery(id+"F10.wireOp",EDGE,"E49.0"),sQuery(id+"F10.wireOp",EDGE,"E59")])]})});
            var Q14;
            Q14=makeQuery(id+"F11.boolean.opBoolean","COPY",EDGE,{"derivedFrom":makeQuery(id+"F11.opExtrude","SWEPT_EDGE",EDGE,{"disambiguationData":[OSD([sQuery(id+"F10.wireOp",EDGE,"E40.right"),sQuery(id+"F10.wireOp",EDGE,"E60")])]})});
            var Q15;
            Q15=makeQuery(id+"F11.boolean.opBoolean","COPY",EDGE,{"derivedFrom":makeQuery(id+"F11.opExtrude","SWEPT_EDGE",EDGE,{"disambiguationData":[OSD([sQuery(id+"F0.wireOp",EDGE,"E0.rect.bottom"),sQuery(id+"F0.wireOp",EDGE,"E0.rect.top"),sQuery(id+"F0.wireOp",EDGE,"E0.rect.left"),sQuery(id+"F0.wireOp",EDGE,"E0.rect.right"),sQuery(id+"F10.wireOp",EDGE,"E58.0")])]})});
            var Q16;
            Q16=makeQuery(id+"F11.boolean.opBoolean","COPY",EDGE,{"derivedFrom":makeQuery(id+"F11.opExtrude","SWEPT_EDGE",EDGE,{"disambiguationData":[OSD([sQuery(id+"F0.wireOp",EDGE,"E0.rect.bottom"),sQuery(id+"F0.wireOp",EDGE,"E0.rect.top"),sQuery(id+"F0.wireOp",EDGE,"E0.rect.left"),sQuery(id+"F0.wireOp",EDGE,"E0.rect.right"),sQuery(id+"F10.wireOp",EDGE,"E48.0")])]})});
            var Q17;
            Q17=makeQuery(id+"F11.boolean.opBoolean","COPY",EDGE,{"derivedFrom":makeQuery(id+"F11.opExtrude","SWEPT_EDGE",EDGE,{"disambiguationData":[OSD([sQuery(id+"F0.wireOp",EDGE,"E0.rect.bottom"),sQuery(id+"F0.wireOp",EDGE,"E0.rect.top"),sQuery(id+"F0.wireOp",EDGE,"E0.rect.left"),sQuery(id+"F0.wireOp",EDGE,"E0.rect.right"),sQuery(id+"F10.wireOp",EDGE,"E48.2")])]})});
            var Q18;
            Q18=makeQuery(id+"F11.boolean.opBoolean","COPY",EDGE,{"derivedFrom":makeQuery(id+"F11.opExtrude","SWEPT_EDGE",EDGE,{"disambiguationData":[OSD([sQuery(id+"F10.wireOp",EDGE,"E48.4"),sQuery(id+"F10.wireOp",EDGE,"E48.5")])]})});
            var Q19;
            Q19=makeQuery(id+"F11.boolean.opBoolean","COPY",EDGE,{"derivedFrom":makeQuery(id+"F11.opExtrude","SWEPT_EDGE",EDGE,{"disambiguationData":[OSD([sQuery(id+"F10.wireOp",EDGE,"E48.2"),sQuery(id+"F10.wireOp",EDGE,"E48.3")])]})});
            var Q20;
            Q20=makeQuery(id+"F11.boolean.opBoolean","COPY",EDGE,{"derivedFrom":makeQuery(id+"F11.opExtrude","SWEPT_EDGE",EDGE,{"disambiguationData":[OSD([sQuery(id+"F10.wireOp",EDGE,"E48.0"),sQuery(id+"F10.wireOp",EDGE,"E48.1")])]})});
            var Q21;
            Q21=makeQuery(id+"F11.boolean.opBoolean","COPY",EDGE,{"derivedFrom":makeQuery(id+"F11.opExtrude","SWEPT_EDGE",EDGE,{"disambiguationData":[OSD([sQuery(id+"F10.wireOp",EDGE,"E58.0"),sQuery(id+"F10.wireOp",EDGE,"E58.1")])]})});
            var Q22;
            Q22=makeQuery(id+"F11.boolean.opBoolean","COPY",EDGE,{"derivedFrom":makeQuery(id+"F11.opExtrude","SWEPT_EDGE",EDGE,{"disambiguationData":[OSD([sQuery(id+"F0.wireOp",EDGE,"E0.rect.bottom"),sQuery(id+"F0.wireOp",EDGE,"E0.rect.top"),sQuery(id+"F0.wireOp",EDGE,"E0.rect.left"),sQuery(id+"F0.wireOp",EDGE,"E0.rect.right"),sQuery(id+"F10.wireOp",EDGE,"E49.2")])]})});
            var Q23;
            Q23=makeQuery(id+"F11.boolean.opBoolean","COPY",EDGE,{"derivedFrom":makeQuery(id+"F11.opExtrude","SWEPT_EDGE",EDGE,{"disambiguationData":[OSD([sQuery(id+"F0.wireOp",EDGE,"E0.rect.bottom"),sQuery(id+"F0.wireOp",EDGE,"E0.rect.top"),sQuery(id+"F0.wireOp",EDGE,"E0.rect.left"),sQuery(id+"F0.wireOp",EDGE,"E0.rect.right"),sQuery(id+"F10.wireOp",EDGE,"E49.4")])]})});
            var Q24;
            Q24=makeQuery(id+"F11.boolean.opBoolean","COPY",EDGE,{"derivedFrom":makeQuery(id+"F11.opExtrude","SWEPT_EDGE",EDGE,{"disambiguationData":[OSD([sQuery(id+"F0.wireOp",EDGE,"E0.rect.bottom"),sQuery(id+"F0.wireOp",EDGE,"E0.rect.top"),sQuery(id+"F0.wireOp",EDGE,"E0.rect.left"),sQuery(id+"F0.wireOp",EDGE,"E0.rect.right"),sQuery(id+"F10.wireOp",EDGE,"E49.6")])]})});
            var Q25;
            Q25=makeQuery(id+"F11.boolean.opBoolean","COPY",EDGE,{"derivedFrom":makeQuery(id+"F11.opExtrude","SWEPT_EDGE",EDGE,{"disambiguationData":[OSD([sQuery(id+"F0.wireOp",EDGE,"E0.rect.bottom"),sQuery(id+"F0.wireOp",EDGE,"E0.rect.top"),sQuery(id+"F0.wireOp",EDGE,"E0.rect.left"),sQuery(id+"F0.wireOp",EDGE,"E0.rect.right"),sQuery(id+"F10.wireOp",EDGE,"E49.0")])]})});
            var Q26;
            Q26=makeQuery(id+"F11.boolean.opBoolean","COPY",EDGE,{"derivedFrom":makeQuery(id+"F11.opExtrude","SWEPT_EDGE",EDGE,{"disambiguationData":[OSD([sQuery(id+"F0.wireOp",EDGE,"E0.rect.bottom"),sQuery(id+"F0.wireOp",EDGE,"E0.rect.top"),sQuery(id+"F0.wireOp",EDGE,"E0.rect.left"),sQuery(id+"F0.wireOp",EDGE,"E0.rect.right"),sQuery(id+"F10.wireOp",EDGE,"E60")])]})});
            var Q27;
            Q27=makeQuery(id+"F11.boolean.opBoolean","COPY",EDGE,{"derivedFrom":makeQuery(id+"F11.opExtrude","SWEPT_EDGE",EDGE,{"disambiguationData":[OSD([sQuery(id+"F0.wireOp",EDGE,"E0.rect.bottom"),sQuery(id+"F0.wireOp",EDGE,"E0.rect.top"),sQuery(id+"F0.wireOp",EDGE,"E0.rect.left"),sQuery(id+"F0.wireOp",EDGE,"E0.rect.right"),sQuery(id+"F10.wireOp",EDGE,"E40.right")])]})});
            var Q28;
            Q28=makeQuery(id+"F11.boolean.opBoolean","COPY",EDGE,{"derivedFrom":makeQuery(id+"F11.opExtrude","SWEPT_EDGE",EDGE,{"disambiguationData":[OSD([sQuery(id+"F0.wireOp",EDGE,"E0.rect.bottom"),sQuery(id+"F0.wireOp",EDGE,"E0.rect.top"),sQuery(id+"F0.wireOp",EDGE,"E0.rect.left"),sQuery(id+"F0.wireOp",EDGE,"E0.rect.right"),sQuery(id+"F10.wireOp",EDGE,"E59")])]})});
            var Q29;
            Q29=makeQuery(id+"F11.boolean.opBoolean","COPY",EDGE,{"derivedFrom":makeQuery(id+"F11.opExtrude","SWEPT_EDGE",EDGE,{"disambiguationData":[OSD([sQuery(id+"F0.wireOp",EDGE,"E0.rect.bottom"),sQuery(id+"F0.wireOp",EDGE,"E0.rect.top"),sQuery(id+"F0.wireOp",EDGE,"E0.rect.left"),sQuery(id+"F0.wireOp",EDGE,"E0.rect.right"),sQuery(id+"F10.wireOp",EDGE,"E49.1")])]})});
            var Q30;
            Q30=makeQuery(id+"F11.boolean.opBoolean","COPY",EDGE,{"derivedFrom":makeQuery(id+"F11.opExtrude","SWEPT_EDGE",EDGE,{"disambiguationData":[OSD([sQuery(id+"F0.wireOp",EDGE,"E0.rect.bottom"),sQuery(id+"F0.wireOp",EDGE,"E0.rect.top"),sQuery(id+"F0.wireOp",EDGE,"E0.rect.left"),sQuery(id+"F0.wireOp",EDGE,"E0.rect.right"),sQuery(id+"F10.wireOp",EDGE,"E49.3")])]})});
            var Q31;
            Q31=makeQuery(id+"F11.boolean.opBoolean","COPY",EDGE,{"derivedFrom":makeQuery(id+"F11.opExtrude","SWEPT_EDGE",EDGE,{"disambiguationData":[OSD([sQuery(id+"F10.wireOp",EDGE,"E40.left"),sQuery(id+"F10.wireOp",EDGE,"E48.6")])]})});
            var Q32;
            Q32=makeQuery(id+"F11.boolean.opBoolean","COPY",EDGE,{"derivedFrom":makeQuery(id+"F11.opExtrude","SWEPT_EDGE",EDGE,{"disambiguationData":[OSD([sQuery(id+"F0.wireOp",EDGE,"E0.rect.bottom"),sQuery(id+"F0.wireOp",EDGE,"E0.rect.top"),sQuery(id+"F0.wireOp",EDGE,"E0.rect.left"),sQuery(id+"F0.wireOp",EDGE,"E0.rect.right"),sQuery(id+"F10.wireOp",EDGE,"E48.4")])]})});
            var Q33;
            Q33=makeQuery(id+"F9.boolean.opBoolean","COPY",EDGE,{"derivedFrom":makeQuery(id+"F9.opExtrude","SWEPT_EDGE",EDGE,{"disambiguationData":[OSD([sQuery(id+"F8.wireOp",EDGE,"E32"),sQuery(id+"F8.wireOp",EDGE,"21a8909e-d1f1-48ab-95bf-b171e8dcea50")])]})});
            var Q34;
            Q34=makeQuery(id+"F9.boolean.opBoolean","COPY",EDGE,{"derivedFrom":makeQuery(id+"F9.opExtrude","SWEPT_EDGE",EDGE,{"disambiguationData":[OSD([sQuery(id+"F8.wireOp",EDGE,"E32"),sQuery(id+"F8.wireOp",EDGE,"1ba8cede-bd71-4284-a01c-5ff4ff7b9d74")])]})});
            var Q35;
            Q35=makeQuery(id+"F9.boolean.opBoolean","COPY",EDGE,{"derivedFrom":makeQuery(id+"F9.opExtrude","SWEPT_EDGE",EDGE,{"disambiguationData":[OSD([sQuery(id+"F8.wireOp",EDGE,"E32"),sQuery(id+"F8.wireOp",EDGE,"169d5384-7eed-4124-bf46-ad3f299ae7b2"),sQuery(id+"F8.wireOp",EDGE,"472916fc-5f19-4337-a011-30199ff5a838")])]})});
            var Q36;
            Q36=makeQuery(id+"F9.boolean.opBoolean","COPY",EDGE,{"derivedFrom":makeQuery(id+"F9.opExtrude","SWEPT_EDGE",EDGE,{"disambiguationData":[OSD([sQuery(id+"F8.wireOp",EDGE,"E22"),sQuery(id+"F8.wireOp",EDGE,"E32"),sQuery(id+"F8.wireOp",EDGE,"ea21bc87-49c2-4c7b-8e74-a24736ba1dfa")])]})});
            var Q37;
            Q37=makeQuery(id+"F9.boolean.opBoolean","COPY",EDGE,{"derivedFrom":makeQuery(id+"F9.opExtrude","SWEPT_EDGE",EDGE,{"disambiguationData":[OSD([sQuery(id+"F8.wireOp",EDGE,"E26"),sQuery(id+"F8.wireOp",EDGE,"169d5384-7eed-4124-bf46-ad3f299ae7b2")])]})});
            var Q38;
            Q38=makeQuery(id+"F9.boolean.opBoolean","COPY",EDGE,{"derivedFrom":makeQuery(id+"F9.opExtrude","SWEPT_EDGE",EDGE,{"disambiguationData":[OSD([sQuery(id+"F8.wireOp",EDGE,"E22"),sQuery(id+"F8.wireOp",EDGE,"E25"),sQuery(id+"F8.wireOp",EDGE,"E26")])]})});
            var Q39;
            Q39=makeQuery(id+"F9.boolean.opBoolean","COPY",EDGE,{"derivedFrom":makeQuery(id+"F9.opExtrude","SWEPT_EDGE",EDGE,{"disambiguationData":[OSD([sQuery(id+"F8.wireOp",EDGE,"E26"),sQuery(id+"F8.wireOp",EDGE,"ea21bc87-49c2-4c7b-8e74-a24736ba1dfa")])]})});
            var Q40;
            Q40=makeQuery(id+"F9.boolean.opBoolean","COPY",EDGE,{"derivedFrom":makeQuery(id+"F9.opExtrude","SWEPT_EDGE",EDGE,{"disambiguationData":[OSD([sQuery(id+"F8.wireOp",EDGE,"E26"),sQuery(id+"F8.wireOp",EDGE,"169d5384-7eed-4124-bf46-ad3f299ae7b2")])]})});
            var Q41;
            Q41=makeQuery(id+"F9.boolean.opBoolean","COPY",EDGE,{"derivedFrom":makeQuery(id+"F9.opExtrude","SWEPT_EDGE",EDGE,{"disambiguationData":[OSD([sQuery(id+"F8.wireOp",EDGE,"E26"),sQuery(id+"F8.wireOp",EDGE,"ea21bc87-49c2-4c7b-8e74-a24736ba1dfa")])]})});
            var Q42;
            Q42=makeQuery(id+"F9.boolean.opBoolean","COPY",EDGE,{"derivedFrom":makeQuery(id+"F9.opExtrude","SWEPT_EDGE",EDGE,{"disambiguationData":[OSD([sQuery(id+"F8.wireOp",EDGE,"E26"),sQuery(id+"F8.wireOp",EDGE,"E27"),sQuery(id+"F8.wireOp",EDGE,"E31")])]})});
            var Q43;
            Q43=makeQuery(id+"F9.boolean.opBoolean","COPY",EDGE,{"derivedFrom":makeQuery(id+"F9.opExtrude","SWEPT_EDGE",EDGE,{"disambiguationData":[OSD([sQuery(id+"F8.wireOp",EDGE,"E26"),sQuery(id+"F8.wireOp",EDGE,"ea21bc87-49c2-4c7b-8e74-a24736ba1dfa")])]})});
            var Q44;
            Q44=makeQuery(id+"F9.boolean.opBoolean","COPY",EDGE,{"derivedFrom":makeQuery(id+"F9.opExtrude","SWEPT_EDGE",EDGE,{"disambiguationData":[OSD([sQuery(id+"F8.wireOp",EDGE,"E26"),sQuery(id+"F8.wireOp",EDGE,"169d5384-7eed-4124-bf46-ad3f299ae7b2")])]})});
            var Q45;
            Q45=makeQuery(id+"F9.boolean.opBoolean","COPY",EDGE,{"derivedFrom":makeQuery(id+"F9.opExtrude","SWEPT_EDGE",EDGE,{"disambiguationData":[OSD([sQuery(id+"F8.wireOp",EDGE,"E31"),sQuery(id+"F8.wireOp",EDGE,"472916fc-5f19-4337-a011-30199ff5a838")])]})});
            var Q46;
            Q46=makeQuery(id+"F9.boolean.opBoolean","COPY",EDGE,{"derivedFrom":makeQuery(id+"F9.opExtrude","SWEPT_EDGE",EDGE,{"disambiguationData":[OSD([sQuery(id+"F8.wireOp",EDGE,"E32"),sQuery(id+"F8.wireOp",EDGE,"1ba8cede-bd71-4284-a01c-5ff4ff7b9d74")])]})});
            var Q47;
            Q47=makeQuery(id+"F9.boolean.opBoolean","COPY",EDGE,{"derivedFrom":makeQuery(id+"F9.opExtrude","SWEPT_EDGE",EDGE,{"disambiguationData":[OSD([sQuery(id+"F8.wireOp",EDGE,"E32"),sQuery(id+"F8.wireOp",EDGE,"21a8909e-d1f1-48ab-95bf-b171e8dcea50")])]})});
            var Q48;
            Q48=makeQuery(id+"F9.boolean.opBoolean","COPY",EDGE,{"derivedFrom":makeQuery(id+"F9.opExtrude","SWEPT_EDGE",EDGE,{"disambiguationData":[OSD([sQuery(id+"F8.wireOp",EDGE,"E32"),sQuery(id+"F8.wireOp",EDGE,"1ba8cede-bd71-4284-a01c-5ff4ff7b9d74")])]})});
            var Q49;
            Q49=makeQuery(id+"F9.boolean.opBoolean","COPY",EDGE,{"derivedFrom":makeQuery(id+"F9.opExtrude","SWEPT_EDGE",EDGE,{"disambiguationData":[OSD([sQuery(id+"F8.wireOp",EDGE,"E31"),sQuery(id+"F8.wireOp",EDGE,"472916fc-5f19-4337-a011-30199ff5a838")])]})});
            var Q50;
            Q50=makeQuery(id+"F9.boolean.opBoolean","COPY",EDGE,{"derivedFrom":makeQuery(id+"F9.opExtrude","SWEPT_EDGE",EDGE,{"disambiguationData":[OSD([sQuery(id+"F8.wireOp",EDGE,"E32"),sQuery(id+"F8.wireOp",EDGE,"21a8909e-d1f1-48ab-95bf-b171e8dcea50")])]})});
            var Q51;
            Q51=makeQuery(id+"F9.boolean.opBoolean","COPY",EDGE,{"derivedFrom":makeQuery(id+"F9.opExtrude","SWEPT_EDGE",EDGE,{"disambiguationData":[OSD([sQuery(id+"F8.wireOp",EDGE,"E32"),sQuery(id+"F8.wireOp",EDGE,"1ba8cede-bd71-4284-a01c-5ff4ff7b9d74")])]})});
            var Q52;
            Q52=makeQuery(id+"F9.boolean.opBoolean","COPY",EDGE,{"derivedFrom":makeQuery(id+"F9.opExtrude","SWEPT_EDGE",EDGE,{"disambiguationData":[OSD([sQuery(id+"F8.wireOp",EDGE,"E32"),sQuery(id+"F8.wireOp",EDGE,"21a8909e-d1f1-48ab-95bf-b171e8dcea50")])]})});
            var Q53;
            Q53=makeQuery(id+"F9.boolean.opBoolean","COPY",EDGE,{"derivedFrom":makeQuery(id+"F9.opExtrude","SWEPT_EDGE",EDGE,{"disambiguationData":[OSD([sQuery(id+"F8.wireOp",EDGE,"E26"),sQuery(id+"F8.wireOp",EDGE,"21a8909e-d1f1-48ab-95bf-b171e8dcea50"),sQuery(id+"F8.wireOp",EDGE,"1ba8cede-bd71-4284-a01c-5ff4ff7b9d74")])]})});
            var Q54;
            Q54=makeQuery(id+"F7.boolean.opBoolean","COPY",EDGE,{"disambiguationData":[OD(0.0)],"derivedFrom":makeQuery(id+"F7.opExtrude","SWEPT_EDGE",EDGE,{"disambiguationData":[OSD([sQuery(id+"F6.wireOp",EDGE,"E6"),sQuery(id+"F6.wireOp",EDGE,"E13")])]})});
            var Q55;
            Q55=makeQuery(id+"F7.boolean.opBoolean","COPY",EDGE,{"disambiguationData":[OD(0.0)],"derivedFrom":makeQuery(id+"F7.opExtrude","SWEPT_EDGE",EDGE,{"disambiguationData":[OSD([sQuery(id+"F6.wireOp",EDGE,"E13"),sQuery(id+"F6.wireOp",EDGE,"E17")])]})});
            var Q56;
            Q56=makeQuery(id+"F7.boolean.opBoolean","COPY",EDGE,{"disambiguationData":[OD(0.0)],"derivedFrom":makeQuery(id+"F7.opExtrude","SWEPT_EDGE",EDGE,{"disambiguationData":[OSD([sQuery(id+"F6.wireOp",EDGE,"E13"),sQuery(id+"F6.wireOp",EDGE,"E20")])]})});
            var Q57;
            Q57=makeQuery(id+"F7.boolean.opBoolean","COPY",EDGE,{"disambiguationData":[OD(0.0)],"derivedFrom":makeQuery(id+"F7.opExtrude","SWEPT_EDGE",EDGE,{"disambiguationData":[OSD([sQuery(id+"F6.wireOp",EDGE,"E5"),sQuery(id+"F6.wireOp",EDGE,"E10"),sQuery(id+"F6.wireOp",EDGE,"E13")])]})});
            var Q58;
            Q58=makeQuery(id+"F7.boolean.opBoolean","COPY",EDGE,{"disambiguationData":[OD(0.0)],"derivedFrom":makeQuery(id+"F7.opExtrude","SWEPT_EDGE",EDGE,{"disambiguationData":[OSD([sQuery(id+"F6.wireOp",EDGE,"E6"),sQuery(id+"F6.wireOp",EDGE,"E13")])]})});
            var Q59;
            Q59=makeQuery(id+"F7.boolean.opBoolean","COPY",EDGE,{"disambiguationData":[OD(0.0)],"derivedFrom":makeQuery(id+"F7.opExtrude","SWEPT_EDGE",EDGE,{"disambiguationData":[OSD([sQuery(id+"F6.wireOp",EDGE,"E6"),sQuery(id+"F6.wireOp",EDGE,"E13")])]})});
            var Q60;
            Q60=makeQuery(id+"F7.boolean.opBoolean","COPY",EDGE,{"disambiguationData":[OD(0.0)],"derivedFrom":makeQuery(id+"F7.opExtrude","SWEPT_EDGE",EDGE,{"disambiguationData":[OSD([sQuery(id+"F6.wireOp",EDGE,"E6"),sQuery(id+"F6.wireOp",EDGE,"E19")])]})});
            var Q61;
            Q61=makeQuery(id+"F7.boolean.opBoolean","COPY",EDGE,{"disambiguationData":[OD(0.0)],"derivedFrom":makeQuery(id+"F7.opExtrude","SWEPT_EDGE",EDGE,{"disambiguationData":[OSD([sQuery(id+"F6.wireOp",EDGE,"E6"),sQuery(id+"F6.wireOp",EDGE,"E20")])]})});
            var Q62;
            Q62=makeQuery(id+"F7.boolean.opBoolean","COPY",EDGE,{"disambiguationData":[OD(0.0)],"derivedFrom":makeQuery(id+"F7.opExtrude","SWEPT_EDGE",EDGE,{"disambiguationData":[OSD([sQuery(id+"F6.wireOp",EDGE,"E5"),sQuery(id+"F6.wireOp",EDGE,"E11")])]})});
            var Q63;
            Q63=makeQuery(id+"F7.boolean.opBoolean","COPY",EDGE,{"disambiguationData":[OD(0.0)],"derivedFrom":makeQuery(id+"F7.opExtrude","SWEPT_EDGE",EDGE,{"disambiguationData":[OSD([sQuery(id+"F6.wireOp",EDGE,"E5"),sQuery(id+"F6.wireOp",EDGE,"E11")])]})});
            var Q64;
            Q64=makeQuery(id+"F7.boolean.opBoolean","COPY",EDGE,{"disambiguationData":[OD(0.0)],"derivedFrom":makeQuery(id+"F7.opExtrude","SWEPT_EDGE",EDGE,{"disambiguationData":[OSD([sQuery(id+"F6.wireOp",EDGE,"E5"),sQuery(id+"F6.wireOp",EDGE,"E11")])]})});
            var Q65;
            Q65=makeQuery(id+"F7.boolean.opBoolean","COPY",EDGE,{"disambiguationData":[OD(0.0)],"derivedFrom":makeQuery(id+"F7.opExtrude","SWEPT_EDGE",EDGE,{"disambiguationData":[OSD([sQuery(id+"F6.wireOp",EDGE,"E5"),sQuery(id+"F6.wireOp",EDGE,"E11")])]})});
            var Q66;
            Q66=makeQuery(id+"F7.boolean.opBoolean","COPY",EDGE,{"disambiguationData":[OD(0.0)],"derivedFrom":makeQuery(id+"F7.opExtrude","SWEPT_EDGE",EDGE,{"disambiguationData":[OSD([sQuery(id+"F6.wireOp",EDGE,"E5"),sQuery(id+"F6.wireOp",EDGE,"E11")])]})});
            var Q67;
            Q67=makeQuery(id+"F7.boolean.opBoolean","COPY",EDGE,{"disambiguationData":[OD(0.0)],"derivedFrom":makeQuery(id+"F7.opExtrude","SWEPT_EDGE",EDGE,{"disambiguationData":[OSD([sQuery(id+"F6.wireOp",EDGE,"E6"),sQuery(id+"F6.wireOp",EDGE,"E13")])]})});
            var Q68;
            Q68=makeQuery(id+"F7.boolean.opBoolean","COPY",EDGE,{"disambiguationData":[OD(0.0)],"derivedFrom":makeQuery(id+"F7.opExtrude","SWEPT_EDGE",EDGE,{"disambiguationData":[OSD([sQuery(id+"F6.wireOp",EDGE,"E13"),sQuery(id+"F6.wireOp",EDGE,"E17")])]})});
            var Q69;
            Q69=makeQuery(id+"F7.boolean.opBoolean","COPY",EDGE,{"disambiguationData":[OD(0.0)],"derivedFrom":makeQuery(id+"F7.opExtrude","SWEPT_EDGE",EDGE,{"disambiguationData":[OSD([sQuery(id+"F6.wireOp",EDGE,"E13"),sQuery(id+"F6.wireOp",EDGE,"E20")])]})});
            var Q70;
            Q70=makeQuery(id+"F7.boolean.opBoolean","COPY",EDGE,{"disambiguationData":[OD(0.0)],"derivedFrom":makeQuery(id+"F7.opExtrude","SWEPT_EDGE",EDGE,{"disambiguationData":[OSD([sQuery(id+"F6.wireOp",EDGE,"E6"),sQuery(id+"F6.wireOp",EDGE,"E13")])]})});
            var Q71;
            Q71=makeQuery(id+"F7.boolean.opBoolean","COPY",EDGE,{"disambiguationData":[OD(0.0)],"derivedFrom":makeQuery(id+"F7.opExtrude","SWEPT_EDGE",EDGE,{"disambiguationData":[OSD([sQuery(id+"F6.wireOp",EDGE,"E13"),sQuery(id+"F6.wireOp",EDGE,"E17")])]})});
            var Q72;
            Q72=makeQuery(id+"F7.boolean.opBoolean","COPY",EDGE,{"disambiguationData":[OD(0.0)],"derivedFrom":makeQuery(id+"F7.opExtrude","SWEPT_EDGE",EDGE,{"disambiguationData":[OSD([sQuery(id+"F6.wireOp",EDGE,"E13"),sQuery(id+"F6.wireOp",EDGE,"E20")])]})});
            var Q73;
            Q73=makeQuery(id+"F7.boolean.opBoolean","COPY",EDGE,{"disambiguationData":[OD(1.0)],"derivedFrom":makeQuery(id+"F7.opExtrude","SWEPT_EDGE",EDGE,{"disambiguationData":[OSD([sQuery(id+"F6.wireOp",EDGE,"E5"),sQuery(id+"F6.wireOp",EDGE,"E11")])]})});
            var Q74;
            Q74=makeQuery(id+"F7.boolean.opBoolean","COPY",EDGE,{"disambiguationData":[OD(1.0)],"derivedFrom":makeQuery(id+"F7.opExtrude","SWEPT_EDGE",EDGE,{"disambiguationData":[OSD([sQuery(id+"F6.wireOp",EDGE,"E5"),sQuery(id+"F6.wireOp",EDGE,"E11")])]})});
            var Q75;
            Q75=makeQuery(id+"F7.boolean.opBoolean","COPY",EDGE,{"disambiguationData":[OD(1.0)],"derivedFrom":makeQuery(id+"F7.opExtrude","SWEPT_EDGE",EDGE,{"disambiguationData":[OSD([sQuery(id+"F6.wireOp",EDGE,"E5"),sQuery(id+"F6.wireOp",EDGE,"E11")])]})});
            var Q76;
            Q76=makeQuery(id+"F7.boolean.opBoolean","COPY",EDGE,{"disambiguationData":[OD(1.0)],"derivedFrom":makeQuery(id+"F7.opExtrude","SWEPT_EDGE",EDGE,{"disambiguationData":[OSD([sQuery(id+"F6.wireOp",EDGE,"E6"),sQuery(id+"F6.wireOp",EDGE,"E19")])]})});
            var Q77;
            Q77=makeQuery(id+"F7.boolean.opBoolean","COPY",EDGE,{"disambiguationData":[OD(1.0)],"derivedFrom":makeQuery(id+"F7.opExtrude","SWEPT_EDGE",EDGE,{"disambiguationData":[OSD([sQuery(id+"F6.wireOp",EDGE,"E6"),sQuery(id+"F6.wireOp",EDGE,"E20")])]})});
            var Q78;
            Q78=makeQuery(id+"F7.boolean.opBoolean","COPY",EDGE,{"disambiguationData":[OD(1.0)],"derivedFrom":makeQuery(id+"F7.opExtrude","SWEPT_EDGE",EDGE,{"disambiguationData":[OSD([sQuery(id+"F6.wireOp",EDGE,"E6"),sQuery(id+"F6.wireOp",EDGE,"E13")])]})});
            var Q79;
            Q79=makeQuery(id+"F7.boolean.opBoolean","COPY",EDGE,{"disambiguationData":[OD(1.0)],"derivedFrom":makeQuery(id+"F7.opExtrude","SWEPT_EDGE",EDGE,{"disambiguationData":[OSD([sQuery(id+"F6.wireOp",EDGE,"E5"),sQuery(id+"F6.wireOp",EDGE,"E11")])]})});
            var Q80;
            Q80=makeQuery(id+"F7.boolean.opBoolean","COPY",EDGE,{"disambiguationData":[OD(1.0)],"derivedFrom":makeQuery(id+"F7.opExtrude","SWEPT_EDGE",EDGE,{"disambiguationData":[OSD([sQuery(id+"F6.wireOp",EDGE,"E5"),sQuery(id+"F6.wireOp",EDGE,"E11")])]})});
            var Q81;
            Q81=makeQuery(id+"F7.boolean.opBoolean","COPY",EDGE,{"disambiguationData":[OD(1.0)],"derivedFrom":makeQuery(id+"F7.opExtrude","SWEPT_EDGE",EDGE,{"disambiguationData":[OSD([sQuery(id+"F6.wireOp",EDGE,"E5"),sQuery(id+"F6.wireOp",EDGE,"E10"),sQuery(id+"F6.wireOp",EDGE,"E13")])]})});
            var Q82;
            Q82=makeQuery(id+"F7.boolean.opBoolean","COPY",EDGE,{"disambiguationData":[OD(1.0)],"derivedFrom":makeQuery(id+"F7.opExtrude","SWEPT_EDGE",EDGE,{"disambiguationData":[OSD([sQuery(id+"F6.wireOp",EDGE,"E6"),sQuery(id+"F6.wireOp",EDGE,"E13")])]})});
            var Q83;
            Q83=makeQuery(id+"F7.boolean.opBoolean","COPY",EDGE,{"disambiguationData":[OD(1.0)],"derivedFrom":makeQuery(id+"F7.opExtrude","SWEPT_EDGE",EDGE,{"disambiguationData":[OSD([sQuery(id+"F6.wireOp",EDGE,"E13"),sQuery(id+"F6.wireOp",EDGE,"E17")])]})});
            var Q84;
            Q84=makeQuery(id+"F7.boolean.opBoolean","COPY",EDGE,{"disambiguationData":[OD(1.0)],"derivedFrom":makeQuery(id+"F7.opExtrude","SWEPT_EDGE",EDGE,{"disambiguationData":[OSD([sQuery(id+"F6.wireOp",EDGE,"E13"),sQuery(id+"F6.wireOp",EDGE,"E20")])]})});
            var Q85;
            Q85=makeQuery(id+"F7.boolean.opBoolean","COPY",EDGE,{"disambiguationData":[OD(1.0)],"derivedFrom":makeQuery(id+"F7.opExtrude","SWEPT_EDGE",EDGE,{"disambiguationData":[OSD([sQuery(id+"F6.wireOp",EDGE,"E6"),sQuery(id+"F6.wireOp",EDGE,"E13")])]})});
            var Q86;
            Q86=makeQuery(id+"F7.boolean.opBoolean","COPY",EDGE,{"disambiguationData":[OD(1.0)],"derivedFrom":makeQuery(id+"F7.opExtrude","SWEPT_EDGE",EDGE,{"disambiguationData":[OSD([sQuery(id+"F6.wireOp",EDGE,"E6"),sQuery(id+"F6.wireOp",EDGE,"E13")])]})});
            var Q87;
            Q87=makeQuery(id+"F7.boolean.opBoolean","COPY",EDGE,{"disambiguationData":[OD(1.0)],"derivedFrom":makeQuery(id+"F7.opExtrude","SWEPT_EDGE",EDGE,{"disambiguationData":[OSD([sQuery(id+"F6.wireOp",EDGE,"E13"),sQuery(id+"F6.wireOp",EDGE,"E17")])]})});
            var Q88;
            Q88=makeQuery(id+"F7.boolean.opBoolean","COPY",EDGE,{"disambiguationData":[OD(1.0)],"derivedFrom":makeQuery(id+"F7.opExtrude","SWEPT_EDGE",EDGE,{"disambiguationData":[OSD([sQuery(id+"F6.wireOp",EDGE,"E13"),sQuery(id+"F6.wireOp",EDGE,"E20")])]})});
            var Q89;
            Q89=makeQuery(id+"F7.boolean.opBoolean","COPY",EDGE,{"disambiguationData":[OD(1.0)],"derivedFrom":makeQuery(id+"F7.opExtrude","SWEPT_EDGE",EDGE,{"disambiguationData":[OSD([sQuery(id+"F6.wireOp",EDGE,"E6"),sQuery(id+"F6.wireOp",EDGE,"E13")])]})});
            var Q90;
            Q90=makeQuery(id+"F7.boolean.opBoolean","COPY",EDGE,{"disambiguationData":[OD(1.0)],"derivedFrom":makeQuery(id+"F7.opExtrude","SWEPT_EDGE",EDGE,{"disambiguationData":[OSD([sQuery(id+"F6.wireOp",EDGE,"E13"),sQuery(id+"F6.wireOp",EDGE,"E17")])]})});
            var Q91;
            Q91=makeQuery(id+"F7.boolean.opBoolean","COPY",EDGE,{"disambiguationData":[OD(1.0)],"derivedFrom":makeQuery(id+"F7.opExtrude","SWEPT_EDGE",EDGE,{"disambiguationData":[OSD([sQuery(id+"F6.wireOp",EDGE,"E13"),sQuery(id+"F6.wireOp",EDGE,"E20")])]})});
            var Q92;
            Q92=makeQuery(id+"F7.boolean.opBoolean","COPY",EDGE,{"disambiguationData":[OD(1.0)],"derivedFrom":makeQuery(id+"F7.opExtrude","SWEPT_EDGE",EDGE,{"disambiguationData":[OSD([sQuery(id+"F6.wireOp",EDGE,"E6"),sQuery(id+"F6.wireOp",EDGE,"E13")])]})});
            var Q93;
            Q93=makeQuery(id+"F7.boolean.opBoolean","COPY",EDGE,{"disambiguationData":[OD(1.0)],"derivedFrom":makeQuery(id+"F7.opExtrude","SWEPT_EDGE",EDGE,{"disambiguationData":[OSD([sQuery(id+"F6.wireOp",EDGE,"E13"),sQuery(id+"F6.wireOp",EDGE,"E17")])]})});
            var Q94;
            Q94=makeQuery(id+"F7.boolean.opBoolean","COPY",EDGE,{"disambiguationData":[OD(1.0)],"derivedFrom":makeQuery(id+"F7.opExtrude","SWEPT_EDGE",EDGE,{"disambiguationData":[OSD([sQuery(id+"F6.wireOp",EDGE,"E13"),sQuery(id+"F6.wireOp",EDGE,"E20")])]})});
            var Q95;
            Q95=makeQuery(id+"F7.boolean.opBoolean","COPY",EDGE,{"disambiguationData":[OD(0.0)],"derivedFrom":makeQuery(id+"F7.opExtrude","SWEPT_EDGE",EDGE,{"disambiguationData":[OSD([sQuery(id+"F6.wireOp",EDGE,"E6"),sQuery(id+"F6.wireOp",EDGE,"E13")])]})});
            var Q96;
            Q96=makeQuery(id+"F7.boolean.opBoolean","COPY",EDGE,{"disambiguationData":[OD(0.0)],"derivedFrom":makeQuery(id+"F7.opExtrude","SWEPT_EDGE",EDGE,{"disambiguationData":[OSD([sQuery(id+"F6.wireOp",EDGE,"E13"),sQuery(id+"F6.wireOp",EDGE,"E17")])]})});
            var Q97;
            Q97=makeQuery(id+"F7.boolean.opBoolean","COPY",EDGE,{"disambiguationData":[OD(0.0)],"derivedFrom":makeQuery(id+"F7.opExtrude","SWEPT_EDGE",EDGE,{"disambiguationData":[OSD([sQuery(id+"F6.wireOp",EDGE,"E13"),sQuery(id+"F6.wireOp",EDGE,"E20")])]})});
            var Q98;
            Q98=makeQuery(id+"F11.boolean.opBoolean","COPY",EDGE,{"derivedFrom":makeQuery(id+"F11.opExtrude","SWEPT_EDGE",EDGE,{"disambiguationData":[OSD([sQuery(id+"F0.wireOp",EDGE,"E0.rect.bottom"),sQuery(id+"F0.wireOp",EDGE,"E0.rect.top"),sQuery(id+"F0.wireOp",EDGE,"E0.rect.left"),sQuery(id+"F0.wireOp",EDGE,"E0.rect.right"),sQuery(id+"F10.wireOp",EDGE,"E49.5")])]})});
            var Q99;
            Q99=makeQuery(id+"F7.boolean.opBoolean","COPY",EDGE,{"disambiguationData":[OD(1.0)],"derivedFrom":makeQuery(id+"F7.opExtrude","SWEPT_EDGE",EDGE,{"disambiguationData":[OSD([sQuery(id+"F6.wireOp",EDGE,"E13"),sQuery(id+"F6.wireOp",EDGE,"E16"),sQuery(id+"F6.wireOp",EDGE,"E19")])]})});
            var Q100;
            Q100=makeQuery(id+"F7.boolean.opBoolean","COPY",EDGE,{"disambiguationData":[OD(1.0)],"derivedFrom":makeQuery(id+"F7.opExtrude","SWEPT_EDGE",EDGE,{"disambiguationData":[OSD([sQuery(id+"F6.wireOp",EDGE,"E5"),sQuery(id+"F6.wireOp",EDGE,"E17")])]})});
            var Q101;
            Q101=makeQuery(id+"F7.boolean.opBoolean","COPY",EDGE,{"disambiguationData":[OD(1.0)],"derivedFrom":makeQuery(id+"F7.opExtrude","SWEPT_EDGE",EDGE,{"disambiguationData":[OSD([sQuery(id+"F6.wireOp",EDGE,"E6"),sQuery(id+"F6.wireOp",EDGE,"E11"),sQuery(id+"F6.wireOp",EDGE,"E12")])]})});
            var Q102;
            Q102=makeQuery(id+"F7.boolean.opBoolean","COPY",EDGE,{"disambiguationData":[OD(0.0)],"derivedFrom":makeQuery(id+"F7.opExtrude","SWEPT_EDGE",EDGE,{"disambiguationData":[OSD([sQuery(id+"F6.wireOp",EDGE,"E13"),sQuery(id+"F6.wireOp",EDGE,"E16"),sQuery(id+"F6.wireOp",EDGE,"E19")])]})});
            var Q103;
            Q103=makeQuery(id+"F7.boolean.opBoolean","COPY",EDGE,{"disambiguationData":[OD(0.0)],"derivedFrom":makeQuery(id+"F7.opExtrude","SWEPT_EDGE",EDGE,{"disambiguationData":[OSD([sQuery(id+"F6.wireOp",EDGE,"E5"),sQuery(id+"F6.wireOp",EDGE,"E17")])]})});
            var Q104;
            Q104=makeQuery(id+"F7.boolean.opBoolean","COPY",EDGE,{"disambiguationData":[OD(0.0)],"derivedFrom":makeQuery(id+"F7.opExtrude","SWEPT_EDGE",EDGE,{"disambiguationData":[OSD([sQuery(id+"F6.wireOp",EDGE,"E6"),sQuery(id+"F6.wireOp",EDGE,"E11"),sQuery(id+"F6.wireOp",EDGE,"E12")])]})});
            var Q105;
            Q105=makeQuery(id+"F9.boolean.opBoolean","COPY",EDGE,{"derivedFrom":makeQuery(id+"F9.opExtrude","SWEPT_EDGE",EDGE,{"disambiguationData":[OSD([sQuery(id+"F8.wireOp",EDGE,"E32"),sQuery(id+"F8.wireOp",EDGE,"E36"),sQuery(id+"F8.wireOp",EDGE,"E37")])]})});
            var Q106;
            Q106=makeQuery(id+"F7.boolean.opBoolean","COPY",EDGE,{"disambiguationData":[OD(1.0)],"derivedFrom":makeQuery(id+"F7.opExtrude","SWEPT_EDGE",EDGE,{"disambiguationData":[OSD([sQuery(id+"F6.wireOp",EDGE,"E5"),sQuery(id+"F6.wireOp",EDGE,"E16")])]})});
            var Q107;
            Q107=makeQuery(id+"F7.boolean.opBoolean","COPY",EDGE,{"disambiguationData":[OD(0.0)],"derivedFrom":makeQuery(id+"F7.opExtrude","SWEPT_EDGE",EDGE,{"disambiguationData":[OSD([sQuery(id+"F6.wireOp",EDGE,"E5"),sQuery(id+"F6.wireOp",EDGE,"E16")])]})});
            fillet(context, id + "F17", {"entities" : qUnion([Q0, Q1, Q2, Q3, Q4, Q5, Q6, Q7, Q8, Q9, Q10, Q11, Q12, Q13, Q14, Q15, Q16, Q17, Q18, Q19, Q20, Q21, Q22, Q23, Q24, Q25, Q26, Q27, Q28, Q29, Q30, Q31, Q32, Q33, Q34, Q35, Q36, Q37, Q38, Q39, Q40, Q41, Q42, Q43, Q44, Q45, Q46, Q47, Q48, Q49, Q50, Q51, Q52, Q53, Q54, Q55, Q56, Q57, Q58, Q59, Q60, Q61, Q62, Q63, Q64, Q65, Q66, Q67, Q68, Q69, Q70, Q71, Q72, Q73, Q74, Q75, Q76, Q77, Q78, Q79, Q80, Q81, Q82, Q83, Q84, Q85, Q86, Q87, Q88, Q89, Q90, Q91, Q92, Q93, Q94, Q95, Q96, Q97, Q98, Q99, Q100, Q101, Q102, Q103, Q104, Q105, Q106, Q107]), "radius" : 2 * mm, "tangentPropagation" : true, "allowEdgeOverflow" : false});
        }
    });
